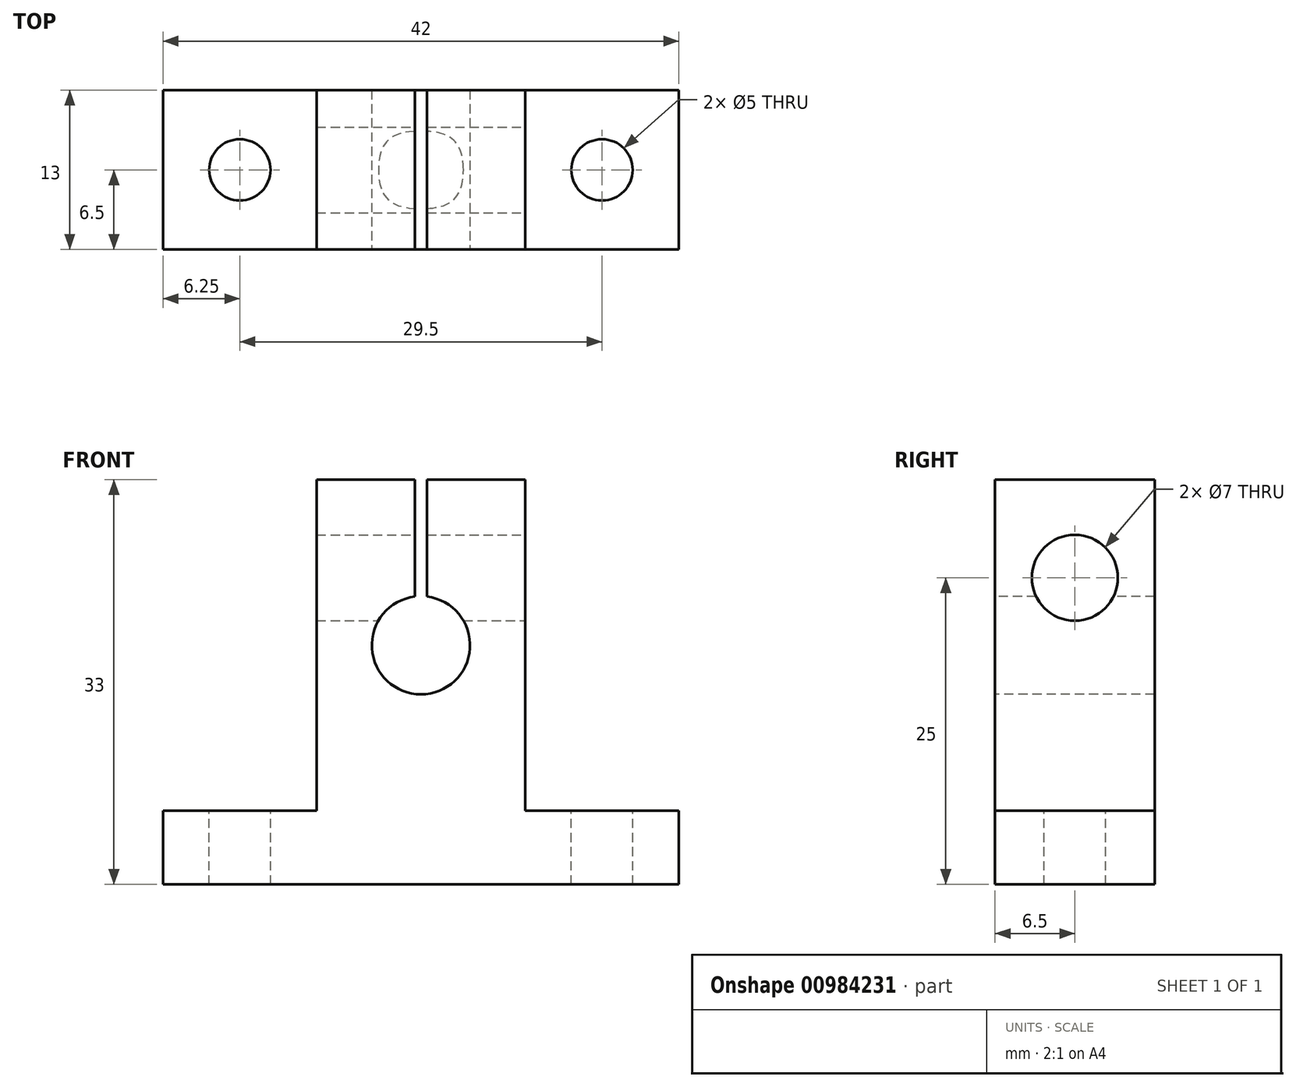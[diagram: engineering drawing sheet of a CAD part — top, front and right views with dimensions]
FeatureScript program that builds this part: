
annotation { "Feature Type Name" : "Feature", "Feature Type Description" : "" }
export const myFeature = defineFeature(function(context is Context, id is Id, definition is map)
    precondition{}
    {
        {
            var Q0;
            Q0=qCreatedBy(makeId("Top.planeOp"),FACE);
            var sketch = newSketch(context, id + "F0", { "sketchPlane" : qUnion([Q0])});
            skLineSegment(sketch, "E0.bottom", {"start": v(-21, 6.5) * mm, "end": v(21, 6.5) * mm});
            skLineSegment(sketch, "E0.top", {"start": v(-21, -6.5) * mm, "end": v(21, -6.5) * mm});
            skLineSegment(sketch, "E0.left", {"start": v(-21, 6.5) * mm, "end": v(-21, -6.5) * mm});
            skLineSegment(sketch, "E0.right", {"start": v(21, 6.5) * mm, "end": v(21, -6.5) * mm});
            skPoint(sketch, "E0.middle", {"position": v(0, 0) * mm});
            skSolve(sketch);
        }
        {
            var Q0;
            Q0 = qSketchRegion(id + "F0", true);
            extrude(context, id + "F1", {"entities" : qUnion([Q0]), "oppositeDirection" : true, "depth" : 6 * mm, "offsetDistance" : 25 * mm});
        }
        {
            var Q0;
            Q0=qCreatedBy(makeId("Top.planeOp"),FACE);
            var sketch = newSketch(context, id + "F2", { "sketchPlane" : qUnion([Q0])});
            skLineSegment(sketch, "E1.bottom", {"start": v(8.5, -6.5) * mm, "end": v(-8.5, -6.5) * mm});
            skLineSegment(sketch, "E1.top", {"start": v(8.5, 6.5) * mm, "end": v(-8.5, 6.5) * mm});
            skLineSegment(sketch, "E1.left", {"start": v(8.5, -6.5) * mm, "end": v(8.5, 6.5) * mm});
            skLineSegment(sketch, "E1.right", {"start": v(-8.5, -6.5) * mm, "end": v(-8.5, 6.5) * mm});
            skPoint(sketch, "E1.middle", {"position": v(0, 0) * mm});
            skSolve(sketch);
        }
        {
            var Q0;
            Q0=qCreatedBy(makeId("Top.planeOp"),FACE);
            var sketch = newSketch(context, id + "F3", { "sketchPlane" : qUnion([Q0])});
            skCircle(sketch, "E2", {"center": v(14.75, 0) * mm, "radius": 2.5 * mm});
            skSolve(sketch);
        }
        {
            var Q0;
            Q0=qCreatedBy(makeId("Top.planeOp"),FACE);
            var sketch = newSketch(context, id + "F4", { "sketchPlane" : qUnion([Q0])});
            skCircle(sketch, "E3", {"center": v(-14.75, 0) * mm, "radius": 2.5 * mm});
            skSolve(sketch);
        }
        {
            var Q0;
            Q0=makeQuery(id+"F2.imprint","IMPRINT",FACE,{"disambiguationData":[TD([[makeQuery(id+"F2.imprint","IMPRINT",EDGE,{"derivedFrom":sQuery(id+"F2.wireOp",EDGE,"E1.bottom")}),-1.0]])]});
            extrude(context, id + "F5", {"entities" : qUnion([Q0]), "operationType" : NewBodyOperationType.ADD, "depth" : 27 * mm, "offsetDistance" : 25 * mm});
        }
        {
            var Q0;
            Q0=makeQuery(id+"F3.imprint","IMPRINT",FACE,{"disambiguationData":[TD([[makeQuery(id+"F3.imprint","IMPRINT",EDGE,{"derivedFrom":sQuery(id+"F3.wireOp",EDGE,"E2")}),1.0]])]});
            extrude(context, id + "F6", {"entities" : qUnion([Q0]), "operationType" : NewBodyOperationType.REMOVE, "oppositeDirection" : true, "depth" : 6 * mm, "offsetDistance" : 25 * mm});
        }
        {
            var Q0;
            Q0=makeQuery(id+"F4.imprint","IMPRINT",FACE,{"disambiguationData":[TD([[makeQuery(id+"F4.imprint","IMPRINT",EDGE,{"derivedFrom":sQuery(id+"F4.wireOp",EDGE,"E3")}),1.0]])]});
            extrude(context, id + "F7", {"entities" : qUnion([Q0]), "operationType" : NewBodyOperationType.REMOVE, "oppositeDirection" : true, "depth" : 6 * mm, "offsetDistance" : 25 * mm});
        }
        {
            var Q0;
            Q0=makeQuery(id+"F5.boolean.opBoolean","MERGE",FACE,{"derivedFrom":[makeQuery(id+"F1.opExtrude","SWEPT_FACE",FACE,{"disambiguationData":[OSD([sQuery(id+"F0.wireOp",EDGE,"E0.top")])]}),makeQuery(id+"F5.opExtrude","SWEPT_FACE",FACE,{"disambiguationData":[OSD([sQuery(id+"F2.wireOp",EDGE,"E1.bottom")])]})]});
            var sketch = newSketch(context, id + "F8", { "sketchPlane" : qUnion([Q0])});
            skCircle(sketch, "E4", {"center": v(0, 13.5) * mm, "radius": 4 * mm});
            skSolve(sketch);
        }
        {
            var Q0;
            Q0=makeQuery(id+"F8.imprint","IMPRINT",FACE,{"disambiguationData":[TD([[makeQuery(id+"F8.imprint","IMPRINT",EDGE,{"derivedFrom":sQuery(id+"F8.wireOp",EDGE,"E4")}),1.0]])]});
            extrude(context, id + "F9", {"entities" : qUnion([Q0]), "operationType" : NewBodyOperationType.REMOVE, "oppositeDirection" : true, "depth" : 15 * mm, "offsetDistance" : 25 * mm});
        }
        {
            var Q0;
            Q0=makeQuery(id+"F5.opExtrude","SWEPT_FACE",FACE,{"disambiguationData":[OSD([sQuery(id+"F2.wireOp",EDGE,"E1.left")])]});
            var sketch = newSketch(context, id + "F10", { "sketchPlane" : qUnion([Q0])});
            skCircle(sketch, "E5", {"center": v(0, 19) * mm, "radius": 3.5 * mm});
            skSolve(sketch);
        }
        {
            var Q0;
            Q0=makeQuery(id+"F10.imprint","IMPRINT",FACE,{"disambiguationData":[TD([[makeQuery(id+"F10.imprint","IMPRINT",EDGE,{"derivedFrom":sQuery(id+"F10.wireOp",EDGE,"E5")}),1.0]])]});
            extrude(context, id + "F11", {"entities" : qUnion([Q0]), "operationType" : NewBodyOperationType.REMOVE, "oppositeDirection" : true, "depth" : 20 * mm, "offsetDistance" : 25 * mm});
        }
        {
            var Q0;
            Q0=makeQuery(id+"F5.opExtrude","CAP_FACE",FACE,{"disambiguationData":[OSD([sQuery(id+"F2.wireOp",EDGE,"E1.bottom"),sQuery(id+"F2.wireOp",EDGE,"E1.top"),sQuery(id+"F2.wireOp",EDGE,"E1.left"),sQuery(id+"F2.wireOp",EDGE,"E1.right")])],"isStart":false});
            var sketch = newSketch(context, id + "F12", { "sketchPlane" : qUnion([Q0])});
            skLineSegment(sketch, "E6.bottom", {"start": v(-0.5, 6.5) * mm, "end": v(0.5, 6.5) * mm});
            skLineSegment(sketch, "E6.top", {"start": v(-0.5, -6.5) * mm, "end": v(0.5, -6.5) * mm});
            skLineSegment(sketch, "E6.left", {"start": v(-0.5, 6.5) * mm, "end": v(-0.5, -6.5) * mm});
            skLineSegment(sketch, "E6.right", {"start": v(0.5, 6.5) * mm, "end": v(0.5, -6.5) * mm});
            skPoint(sketch, "E6.middle", {"position": v(0, 0) * mm});
            skSolve(sketch);
        }
        {
            var Q0;
            Q0=makeQuery(id+"F12.imprint","IMPRINT",FACE,{"disambiguationData":[TD([[makeQuery(id+"F12.imprint","IMPRINT",EDGE,{"derivedFrom":sQuery(id+"F12.wireOp",EDGE,"E6.bottom")}),1.0]])]});
            extrude(context, id + "F13", {"entities" : qUnion([Q0]), "operationType" : NewBodyOperationType.REMOVE, "oppositeDirection" : true, "depth" : 13 * mm, "offsetDistance" : 25 * mm});
        }
    });
